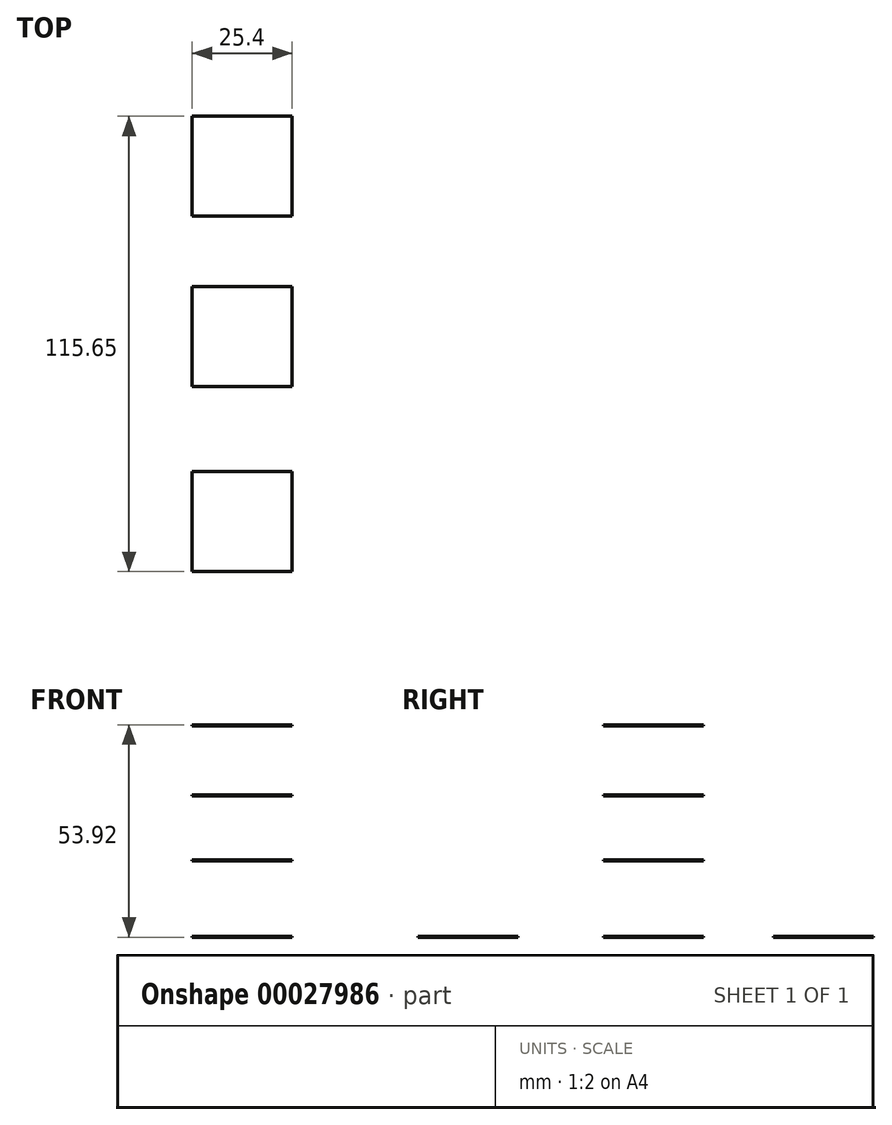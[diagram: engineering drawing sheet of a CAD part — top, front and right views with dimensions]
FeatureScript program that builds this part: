
annotation { "Feature Type Name" : "Feature", "Feature Type Description" : "" }
export const myFeature = defineFeature(function(context is Context, id is Id, definition is map)
    precondition{}
    {
        {
            var Q0;
            Q0=qCreatedBy(makeId("Top.planeOp"),FACE);
            var sketch = newSketch(context, id + "F0", { "sketchPlane" : qUnion([Q0])});
            skLineSegment(sketch, "E0.rect.bottom", {"start": v(-12.7, 12.7) * mm, "end": v(12.7, 12.7) * mm});
            skLineSegment(sketch, "E0.rect.top", {"start": v(-12.7, -12.7) * mm, "end": v(12.7, -12.7) * mm});
            skLineSegment(sketch, "E0.rect.left", {"start": v(-12.7, 12.7) * mm, "end": v(-12.7, -12.7) * mm});
            skLineSegment(sketch, "E0.rect.right", {"start": v(12.7, 12.7) * mm, "end": v(12.7, -12.7) * mm});
            skPoint(sketch, "E0.rect.middle", {"position": v(0, 0) * mm});
            skSolve(sketch);
        }
        {
            var Q0;
            Q0=makeQuery(id+"F0.imprint","IMPRINT",FACE,{"disambiguationData":[TD([[makeQuery(id+"F0.imprint","IMPRINT",EDGE,{"derivedFrom":sQuery(id+"F0.wireOp",EDGE,"E0.rect.bottom")}),-1.0]])]});
            extrude(context, id + "F1", {"entities" : qUnion([Q0]), "depth" : 0.25 * mm});
        }
        {
            var Q0;
            Q0=makeQuery(id+"F1.opExtrude","SWEPT_BODY",BODY,{"disambiguationData":[OSD([sQuery(id+"F0.wireOp",EDGE,"E0.rect.bottom"),sQuery(id+"F0.wireOp",EDGE,"E0.rect.top"),sQuery(id+"F0.wireOp",EDGE,"E0.rect.left"),sQuery(id+"F0.wireOp",EDGE,"E0.rect.right")])]});
            transform(context, id + "F2", {"entities" : qUnion([Q0]), "transformType" : TransformType.TRANSLATION_3D, "dx" : 0 * mm, "dy" : 0 * mm, "dz" : 19.43 * mm, "makeCopy" : true});
        }
        {
            var Q0;
            Q0=makeQuery(id+"F1.opExtrude","SWEPT_BODY",BODY,{"disambiguationData":[OSD([sQuery(id+"F0.wireOp",EDGE,"E0.rect.bottom"),sQuery(id+"F0.wireOp",EDGE,"E0.rect.top"),sQuery(id+"F0.wireOp",EDGE,"E0.rect.left"),sQuery(id+"F0.wireOp",EDGE,"E0.rect.right")])]});
            transform(context, id + "F3", {"entities" : qUnion([Q0]), "transformType" : TransformType.TRANSLATION_3D, "dx" : 0 * mm, "dy" : 0 * mm, "dz" : 35.86 * mm, "makeCopy" : true});
        }
        {
            var Q0;
            Q0=makeQuery(id+"F1.opExtrude","SWEPT_BODY",BODY,{"disambiguationData":[OSD([sQuery(id+"F0.wireOp",EDGE,"E0.rect.bottom"),sQuery(id+"F0.wireOp",EDGE,"E0.rect.top"),sQuery(id+"F0.wireOp",EDGE,"E0.rect.left"),sQuery(id+"F0.wireOp",EDGE,"E0.rect.right")])]});
            transform(context, id + "F4", {"entities" : qUnion([Q0]), "transformType" : TransformType.TRANSLATION_3D, "dx" : 0 * mm, "dy" : 0 * mm, "dz" : 53.67 * mm, "makeCopy" : true});
        }
        {
            var Q0;
            Q0=makeQuery(id+"F1.opExtrude","SWEPT_BODY",BODY,{"disambiguationData":[OSD([sQuery(id+"F0.wireOp",EDGE,"E0.rect.bottom"),sQuery(id+"F0.wireOp",EDGE,"E0.rect.top"),sQuery(id+"F0.wireOp",EDGE,"E0.rect.left"),sQuery(id+"F0.wireOp",EDGE,"E0.rect.right")])]});
            transform(context, id + "F5", {"entities" : qUnion([Q0]), "transformType" : TransformType.TRANSLATION_3D, "dx" : 0 * mm, "dy" : 43.2 * mm, "dz" : 0 * mm, "makeCopy" : true});
        }
        {
            var Q0;
            Q0=makeQuery(id+"F1.opExtrude","SWEPT_BODY",BODY,{"disambiguationData":[OSD([sQuery(id+"F0.wireOp",EDGE,"E0.rect.bottom"),sQuery(id+"F0.wireOp",EDGE,"E0.rect.top"),sQuery(id+"F0.wireOp",EDGE,"E0.rect.left"),sQuery(id+"F0.wireOp",EDGE,"E0.rect.right")])]});
            transform(context, id + "F6", {"entities" : qUnion([Q0]), "transformType" : TransformType.TRANSLATION_3D, "dx" : 0 * mm, "dy" : -47.05 * mm, "dz" : 0 * mm, "makeCopy" : true});
        }
    });
